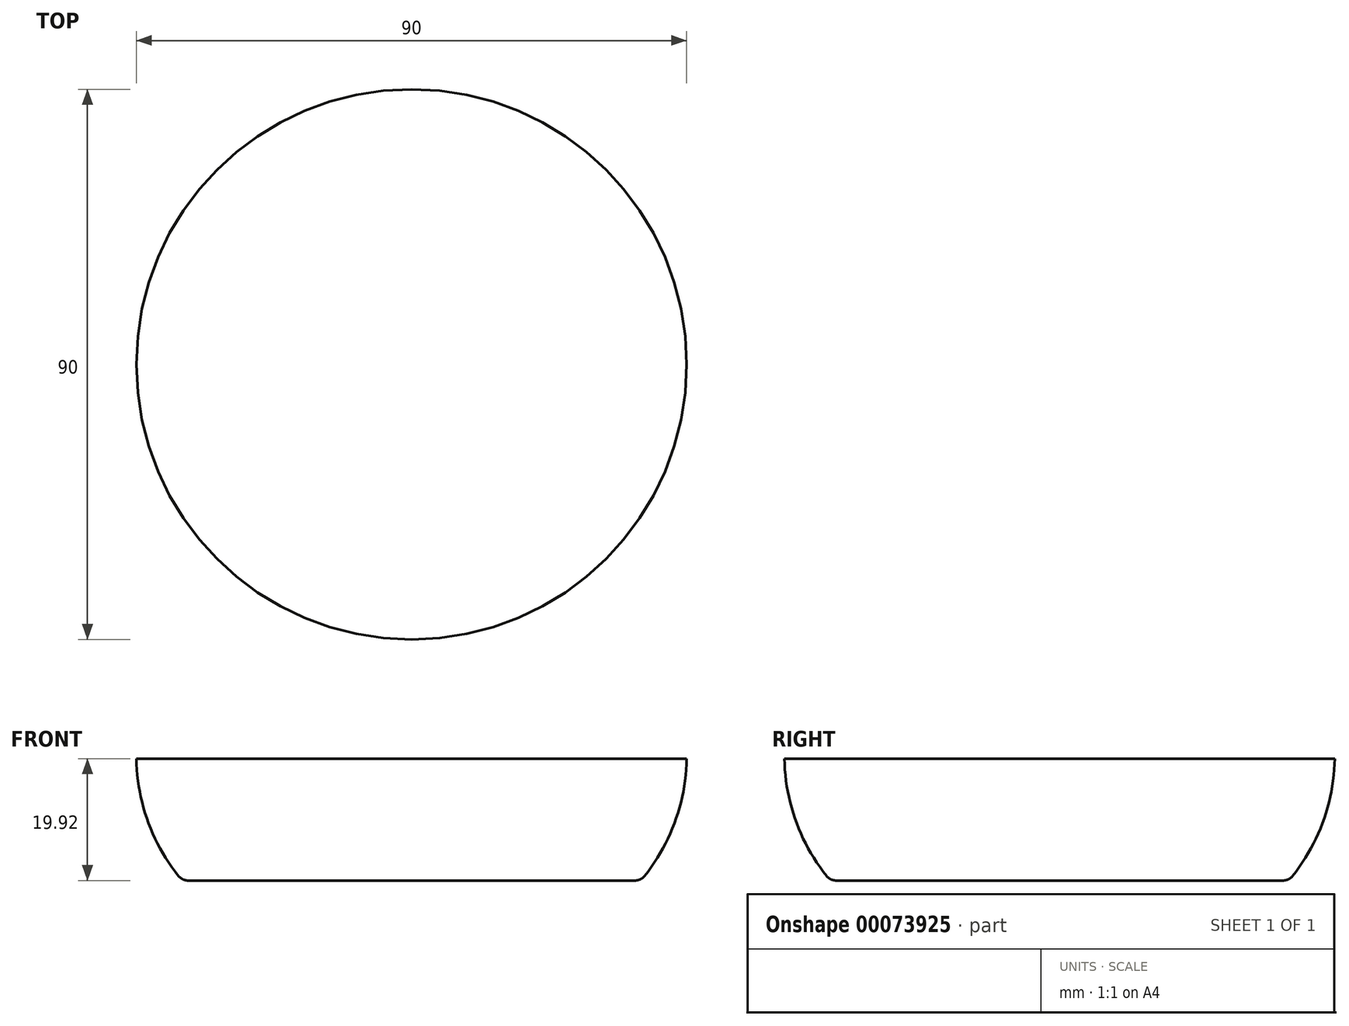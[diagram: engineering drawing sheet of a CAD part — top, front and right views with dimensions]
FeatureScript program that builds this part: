
annotation { "Feature Type Name" : "Feature", "Feature Type Description" : "" }
export const myFeature = defineFeature(function(context is Context, id is Id, definition is map)
    precondition{}
    {
        {
            var Q0;
            Q0=qCreatedBy(makeId("Top.planeOp"),FACE);
            cPlane(context, id + "F0", {"entities" : qUnion([Q0]), "cplaneType" : CPlaneType.OFFSET, "offset" : 20 * mm, "oppositeDirection" : true, "width" : 150 * mm, "height" : 150 * mm});
        }
        {
            var Q0;
            Q0=qCreatedBy(makeId("Front.planeOp"),FACE);
            var sketch = newSketch(context, id + "F1", { "sketchPlane" : qUnion([Q0])});
            skLineSegment(sketch, "E0", {"start": v(0, 0) * mm, "end": v(-45, 0) * mm});
            skLineSegment(sketch, "E1", {"start": v(0, -19.92) * mm, "end": v(-37.5, -19.92) * mm});
            skArc(sketch, "E2", {"start": v(-45, 0) * mm, "mid": v(-42.98, -10.61) * mm, "end": v(-37.5, -19.92) * mm});
            skLineSegment(sketch, "E3", {"start": v(0, 0) * mm, "end": v(0, -19.92) * mm});
            skSolve(sketch);
        }
        {
            var Q0;
            Q0=makeQuery(id+"F1.imprint","IMPRINT",FACE,{"disambiguationData":[TD([[makeQuery(id+"F1.imprint","IMPRINT",EDGE,{"derivedFrom":sQuery(id+"F1.wireOp",EDGE,"E0")}),1.0]])]});
            var Q1;
            Q1=sQuery(id+"F1.wireOp",EDGE,"E3");
            revolve(context, id + "F2", {"entities" : qUnion([Q0]), "axis" : qUnion([Q1]), "revolveType" : RevolveType.FULL});
        }
        {
            var Q0;
            Q0=makeQuery(id+"F2.opRevolve","SWEPT_EDGE",EDGE,{"disambiguationData":[OSD([sQuery(id+"F1.wireOp",EDGE,"E1"),sQuery(id+"F1.wireOp",EDGE,"E2")])]});
            fillet(context, id + "F3", {"entities" : qUnion([Q0]), "radius" : 2 * mm, "tangentPropagation" : true, "allowEdgeOverflow" : false});
        }
    });
